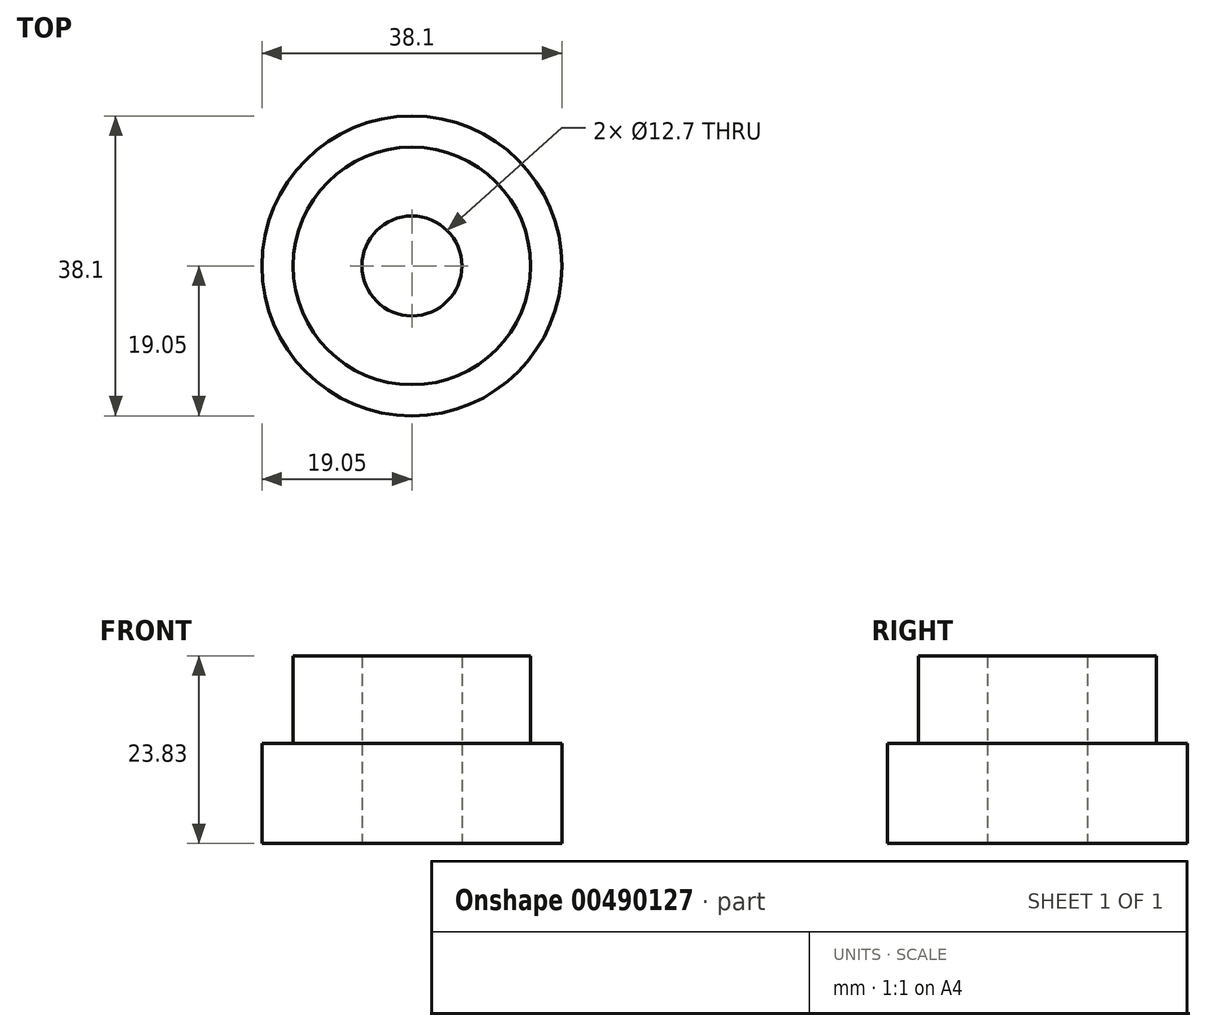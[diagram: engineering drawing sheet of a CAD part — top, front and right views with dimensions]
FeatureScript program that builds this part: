
annotation { "Feature Type Name" : "Feature", "Feature Type Description" : "" }
export const myFeature = defineFeature(function(context is Context, id is Id, definition is map)
    precondition{}
    {
        {
            var Q0;
            Q0=qCreatedBy(makeId("Top.planeOp"),FACE);
            var sketch = newSketch(context, id + "F0", { "sketchPlane" : qUnion([Q0])});
            skCircle(sketch, "E0", {"center": v(0, 0) * mm, "radius": 19.05 * mm});
            skSolve(sketch);
        }
        {
            var Q0;
            Q0=makeQuery(id+"F0.imprint","IMPRINT",FACE,{"disambiguationData":[TD([[makeQuery(id+"F0.imprint","IMPRINT",EDGE,{"derivedFrom":sQuery(id+"F0.wireOp",EDGE,"E0")}),1.0]])]});
            extrude(context, id + "F1", {"entities" : qUnion([Q0]), "depth" : 12.7 * mm});
        }
        {
            var Q0;
            Q0=makeQuery(id+"F1.opExtrude","CAP_FACE",FACE,{"disambiguationData":[OSD([sQuery(id+"F0.wireOp",EDGE,"E0")])],"isStart":false});
            var sketch = newSketch(context, id + "F2", { "sketchPlane" : qUnion([Q0])});
            skCircle(sketch, "E1", {"center": v(0, 0) * mm, "radius": 15.09 * mm});
            skSolve(sketch);
        }
        {
            var Q0;
            Q0=makeQuery(id+"F2.imprint","IMPRINT",FACE,{"disambiguationData":[TD([[makeQuery(id+"F2.imprint","IMPRINT",EDGE,{"derivedFrom":sQuery(id+"F2.wireOp",EDGE,"E1")}),1.0]])]});
            var Q1;
            Q1=sQuery(id+"F2.wireOp",EDGE,"E1");
            extrude(context, id + "F3", {"entities" : qUnion([Q0]), "surfaceEntities" : qUnion([Q1]), "depth" : 11.13 * mm});
        }
        {
            var Q0;
            Q0=makeQuery(id+"F1.opExtrude","CAP_FACE",FACE,{"disambiguationData":[OSD([sQuery(id+"F0.wireOp",EDGE,"E0")])],"isStart":true});
            var sketch = newSketch(context, id + "F4", { "sketchPlane" : qUnion([Q0])});
            skCircle(sketch, "E2", {"center": v(0, 0) * mm, "radius": 6.35 * mm});
            skSolve(sketch);
        }
        {
            var Q0;
            Q0=sQuery(id+"F4.wireOp",VERTEX,"E2.center");
            var Q1;
            Q1=makeQuery(id+"F1.opExtrude","SWEPT_BODY",BODY,{"disambiguationData":[OSD([sQuery(id+"F0.wireOp",EDGE,"E0")])]});
            var Q2;
            Q2=makeQuery(id+"F3.opExtrude","SWEPT_BODY",BODY,{"disambiguationData":[OSD([sQuery(id+"F2.wireOp",EDGE,"E1")])]});
            hole(context, id + "F5", {"style" : HoleStyle.SIMPLE, "endStyle" : HoleEndStyle.THROUGH, "holeDiameter" : 12.7 * mm, "isTappedThrough" : true, "tappedDepth" : 12.7 * mm, "tapClearance" : 3, "locations" : qUnion([Q0]), "scope" : qUnion([Q1, Q2])});
        }
    });
